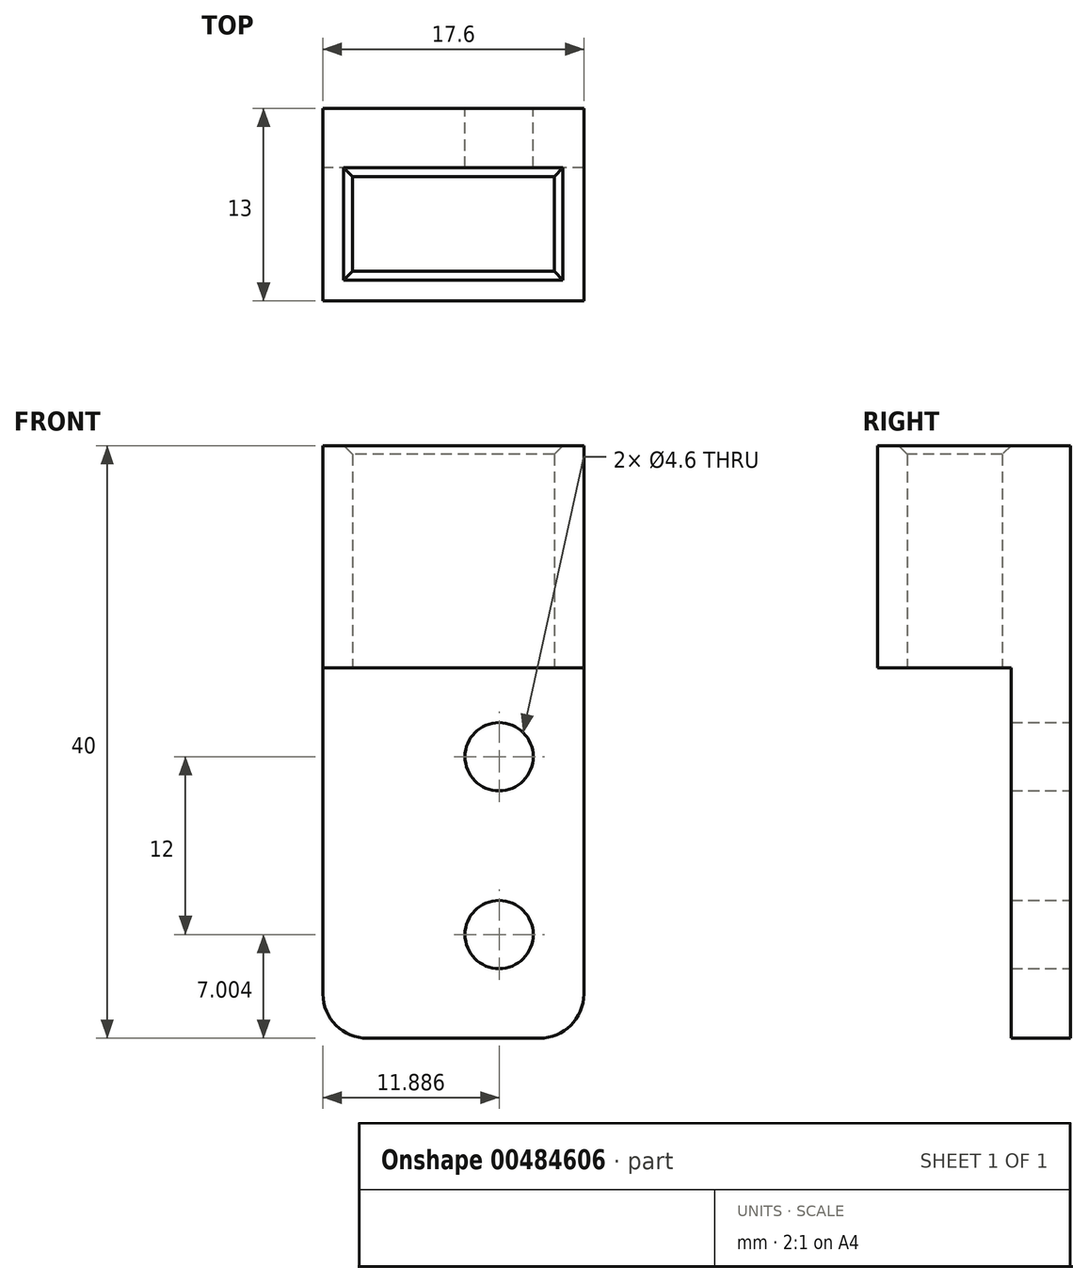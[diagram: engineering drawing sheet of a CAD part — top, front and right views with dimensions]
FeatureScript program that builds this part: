
annotation { "Feature Type Name" : "Feature", "Feature Type Description" : "" }
export const myFeature = defineFeature(function(context is Context, id is Id, definition is map)
    precondition{}
    {
        {
            var Q0;
            Q0=qCreatedBy(makeId("Top.planeOp"),FACE);
            var sketch = newSketch(context, id + "F0", { "sketchPlane" : qUnion([Q0])});
            skLineSegment(sketch, "E0.bottom", {"start": v(-12.09, 6.32) * mm, "end": v(1.51, 6.32) * mm});
            skLineSegment(sketch, "E0.top", {"start": v(-12.09, -0.08) * mm, "end": v(1.51, -0.08) * mm});
            skLineSegment(sketch, "E0.left", {"start": v(-12.09, 6.32) * mm, "end": v(-12.09, -0.08) * mm});
            skLineSegment(sketch, "E0.right", {"start": v(1.51, 6.32) * mm, "end": v(1.51, -0.08) * mm});
            skLineSegment(sketch, "E1.bottom", {"start": v(-14.09, 6.92) * mm, "end": v(3.51, 6.92) * mm});
            skLineSegment(sketch, "E1.top", {"start": v(-14.09, -2.08) * mm, "end": v(3.51, -2.08) * mm});
            skLineSegment(sketch, "E1.left", {"start": v(-14.09, 6.92) * mm, "end": v(-14.09, -2.08) * mm});
            skLineSegment(sketch, "E1.right", {"start": v(3.51, 6.92) * mm, "end": v(3.51, -2.08) * mm});
            skSolve(sketch);
        }
        {
            var Q0;
            Q0=qSketchRegion(id+"F0",true);
            var Q1;
            Q1=makeQuery(id+"F0.imprint","IMPRINT",FACE,{"disambiguationData":[TD([[makeQuery(id+"F0.imprint","IMPRINT",EDGE,{"derivedFrom":sQuery(id+"F0.wireOp",EDGE,"E0.bottom")}),1.0]])]});
            extrude(context, id + "F1", {"entities" : qUnion([Q0, Q1]), "depth" : 15 * mm, "offsetDistance" : 25 * mm, "symmetric" : true});
        }
        {
            var Q0;
            Q0=makeQuery(id+"F1.opExtrude","SWEPT_FACE",FACE,{"disambiguationData":[OSD([sQuery(id+"F0.wireOp",EDGE,"E1.bottom")])]});
            var sketch = newSketch(context, id + "F2", { "sketchPlane" : qUnion([Q0])});
            skLineSegment(sketch, "E2.bottom", {"start": v(14.09, 7.5) * mm, "end": v(-3.51, 7.5) * mm});
            skLineSegment(sketch, "E2.right", {"start": v(-3.51, 7.5) * mm, "end": v(-3.51, -32.5) * mm});
            skLineSegment(sketch, "E3", {"start": v(14.09, 7.5) * mm, "end": v(14.09, -32.5) * mm});
            skLineSegment(sketch, "E4", {"start": v(14.09, -32.5) * mm, "end": v(-3.51, -32.5) * mm});
            skPoint(sketch, "E5", {"position": v(2.2, -13.5) * mm});
            skPoint(sketch, "E5.positionSnap0", {"position": v(2.2, -32.5) * mm});
            skPoint(sketch, "E6", {"position": v(2.2, -25.5) * mm});
            skSolve(sketch);
        }
        {
            var Q0;
            {var subQ0=sQuery(id+"F2.wireOp",EDGE,"E2.top");Q0=makeQuery(id+"F2.imprint","IMPRINT",FACE,{"disambiguationData":[TD([[makeQuery(id+"F2.imprint","IMPRINT",EDGE,{"derivedFrom":subQ0}),-1.0]])]});}
            var Q1;
            {var subQ3=sQuery(id+"F2.wireOp",EDGE,"E3");Q1=makeQuery(id+"F2.imprint","IMPRINT",FACE,{"disambiguationData":[TD([[makeQuery(id+"F2.imprint","IMPRINT",EDGE,{"derivedFrom":subQ3}),-1.0]])]});}
            extrude(context, id + "F3", {"entities" : qUnion([Q0, Q1]), "operationType" : NewBodyOperationType.ADD, "depth" : 4 * mm, "offsetDistance" : 25 * mm});
        }
        {
            var Q0;
            Q0=makeQuery(id+"F1.opExtrude","CAP_EDGE",EDGE,{"disambiguationData":[OSD([sQuery(id+"F0.wireOp",EDGE,"E0.bottom")])],"isStart":false});
            var Q1;
            Q1=makeQuery(id+"F1.opExtrude","CAP_EDGE",EDGE,{"disambiguationData":[OSD([sQuery(id+"F0.wireOp",EDGE,"E0.right")])],"isStart":false});
            var Q2;
            Q2=makeQuery(id+"F1.opExtrude","CAP_EDGE",EDGE,{"disambiguationData":[OSD([sQuery(id+"F0.wireOp",EDGE,"E0.left")])],"isStart":false});
            var Q3;
            Q3=makeQuery(id+"F1.opExtrude","CAP_EDGE",EDGE,{"disambiguationData":[OSD([sQuery(id+"F0.wireOp",EDGE,"E0.top")])],"isStart":false});
            chamfer(context, id + "F4", {"entities" : qUnion([Q0, Q1, Q2, Q3]), "width" : 0.6 * mm, "tangentPropagation" : true});
        }
        {
            var Q0;
            Q0=sQuery(id+"F2.wireOp",VERTEX,"E6");
            var Q1;
            Q1=sQuery(id+"F2.wireOp",VERTEX,"E5");
            var Q2;
            Q2=makeQuery(id+"F1.opExtrude","SWEPT_BODY",BODY,{"disambiguationData":[OSD([sQuery(id+"F0.wireOp",EDGE,"E0.bottom"),sQuery(id+"F0.wireOp",EDGE,"E0.top"),sQuery(id+"F0.wireOp",EDGE,"E0.left"),sQuery(id+"F0.wireOp",EDGE,"E0.right"),sQuery(id+"F0.wireOp",EDGE,"E1.bottom"),sQuery(id+"F0.wireOp",EDGE,"E1.top"),sQuery(id+"F0.wireOp",EDGE,"E1.left"),sQuery(id+"F0.wireOp",EDGE,"E1.right")])]});
            hole(context, id + "F5", {"style" : HoleStyle.SIMPLE, "endStyle" : HoleEndStyle.BLIND, "oppositeDirection" : true, "holeDiameter" : 4.6 * mm, "majorDiameter" : 5 * mm, "holeDepth" : 10 * mm, "isTappedThrough" : true, "tappedDepth" : 7 * mm, "tapClearance" : 6, "locations" : qUnion([Q0, Q1]), "scope" : qUnion([Q2]), "startStyle" : HoleStartStyle.SKETCH});
        }
        {
            var Q0;
            Q0=makeQuery(id+"F3.opExtrude","SWEPT_EDGE",EDGE,{"disambiguationData":[OSD([sQuery(id+"F2.wireOp",EDGE,"E2.right"),sQuery(id+"F2.wireOp",EDGE,"E4")])]});
            var Q1;
            Q1=makeQuery(id+"F3.opExtrude","SWEPT_EDGE",EDGE,{"disambiguationData":[OSD([sQuery(id+"F2.wireOp",EDGE,"E3"),sQuery(id+"F2.wireOp",EDGE,"E4")])]});
            fillet(context, id + "F6", {"entities" : qUnion([Q0, Q1]), "radius" : 3 * mm, "tangentPropagation" : true, "allowEdgeOverflow" : false});
        }
    });
